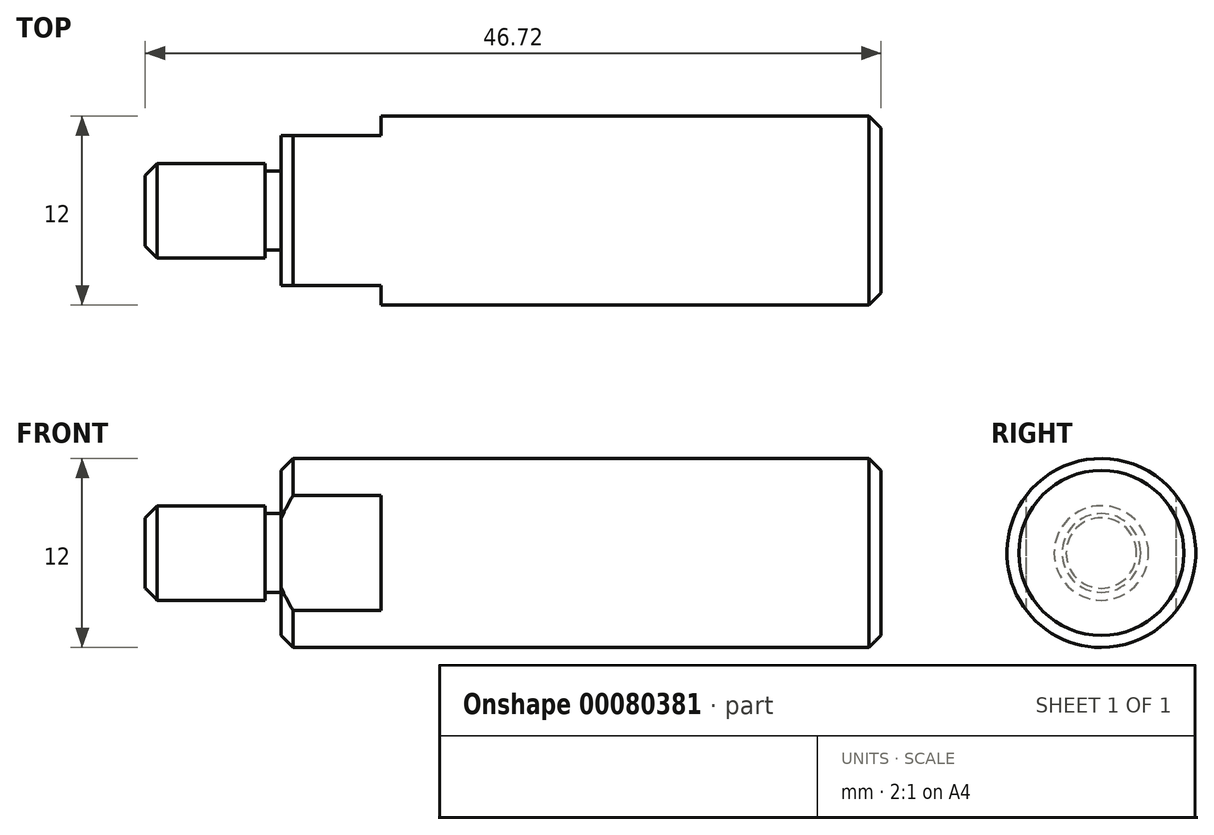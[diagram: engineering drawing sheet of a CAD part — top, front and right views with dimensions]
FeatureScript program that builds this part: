
annotation { "Feature Type Name" : "Feature", "Feature Type Description" : "" }
export const myFeature = defineFeature(function(context is Context, id is Id, definition is map)
    precondition{}
    {
        {
            var Q0;
            Q0=qCreatedBy(makeId("Right.planeOp"),FACE);
            var sketch = newSketch(context, id + "F0", { "sketchPlane" : qUnion([Q0])});
            skCircle(sketch, "E0", {"center": v(0, 0) * mm, "radius": 3 * mm});
            skSolve(sketch);
        }
        {
            var Q0;
            Q0 = qSketchRegion(id + "F0", true);
            extrude(context, id + "F1", {"entities" : qUnion([Q0]), "oppositeDirection" : true, "depth" : 7.62 * mm});
        }
        {
            var Q0;
            Q0=qCreatedBy(makeId("Right.planeOp"),FACE);
            var sketch = newSketch(context, id + "F2", { "sketchPlane" : qUnion([Q0])});
            skCircle(sketch, "E1", {"center": v(0, 0) * mm, "radius": 2.5 * mm});
            skSolve(sketch);
        }
        {
            var Q0;
            Q0 = qSketchRegion(id + "F2", true);
            extrude(context, id + "F3", {"entities" : qUnion([Q0]), "operationType" : NewBodyOperationType.ADD, "depth" : 1 * mm});
        }
        {
            var Q0;
            Q0=makeQuery(id+"F3.opExtrude","CAP_FACE",FACE,{"disambiguationData":[OSD([sQuery(id+"F2.wireOp",EDGE,"E1")])],"isStart":false});
            var sketch = newSketch(context, id + "F4", { "sketchPlane" : qUnion([Q0])});
            skCircle(sketch, "E2", {"center": v(0, 0) * mm, "radius": 6 * mm});
            skSolve(sketch);
        }
        {
            var Q0;
            Q0 = qSketchRegion(id + "F4", true);
            extrude(context, id + "F5", {"entities" : qUnion([Q0]), "operationType" : NewBodyOperationType.ADD, "depth" : 38.1 * mm});
        }
        {
            var Q0;
            Q0=makeQuery(id+"F1.opExtrude","CAP_FACE",FACE,{"disambiguationData":[OSD([sQuery(id+"F0.wireOp",EDGE,"E0")])],"isStart":false});
            var Q1;
            Q1=makeQuery(id+"F5.opExtrude","CAP_EDGE",EDGE,{"disambiguationData":[OSD([sQuery(id+"F4.wireOp",EDGE,"E2")])],"isStart":true});
            var Q2;
            Q2=makeQuery(id+"F5.opExtrude","CAP_EDGE",EDGE,{"disambiguationData":[OSD([sQuery(id+"F4.wireOp",EDGE,"E2")])],"isStart":false});
            chamfer(context, id + "F6", {"entities" : qUnion([Q0, Q1, Q2]), "width" : 0.76 * mm, "tangentPropagation" : true});
        }
        {
            var Q0;
            Q0=makeQuery(id+"F5.opExtrude","CAP_FACE",FACE,{"disambiguationData":[OSD([sQuery(id+"F4.wireOp",EDGE,"E2")])],"isStart":true});
            var sketch = newSketch(context, id + "F7", { "sketchPlane" : qUnion([Q0])});
            skLineSegment(sketch, "E3", {"start": v(0, -31.32) * mm, "end": v(0, 18) * mm, "construction": true});
            skLineSegment(sketch, "E4.0", {"start": v(-4.76, -31.32) * mm, "end": v(-4.76, 18) * mm, "construction": true});
            skLineSegment(sketch, "E5.bottom", {"start": v(-4.76, -17.84) * mm, "end": v(-20.73, -17.84) * mm});
            skLineSegment(sketch, "E5.top", {"start": v(-4.76, 18.85) * mm, "end": v(-20.73, 18.85) * mm});
            skLineSegment(sketch, "E5.left", {"start": v(-4.76, -17.84) * mm, "end": v(-4.76, 18.85) * mm});
            skLineSegment(sketch, "E5.right", {"start": v(-20.73, -17.84) * mm, "end": v(-20.73, 18.85) * mm});
            skLineSegment(sketch, "E6.MirrorCS", {"start": v(4.76, -17.84) * mm, "end": v(20.73, -17.84) * mm});
            skLineSegment(sketch, "E7.MirrorCS", {"start": v(20.73, -17.84) * mm, "end": v(20.73, 18.85) * mm});
            skLineSegment(sketch, "E8.MirrorCS", {"start": v(4.76, -17.84) * mm, "end": v(4.76, 18.85) * mm});
            skLineSegment(sketch, "E9.MirrorCS", {"start": v(4.76, 18.85) * mm, "end": v(20.73, 18.85) * mm});
            skSolve(sketch);
        }
        {
            var Q0;
            Q0 = qSketchRegion(id + "F7", true);
            extrude(context, id + "F8", {"entities" : qUnion([Q0]), "operationType" : NewBodyOperationType.REMOVE, "oppositeDirection" : true, "depth" : 6.35 * mm});
        }
    });
